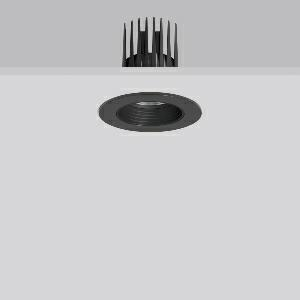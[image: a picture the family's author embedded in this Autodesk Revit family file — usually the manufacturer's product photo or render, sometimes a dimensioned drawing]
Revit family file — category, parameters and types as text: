
# Revit family: heledon_mini_e_901747_003_2_76_4866
name_source: partatom
category: Lighting Fixtures
units: mm (PartAtom-declared; Revit-internal decimal feet)

## family parameters
Cut with Voids When Loaded = No
Host = Face
Light Source = No
Part Type = Normal
Room Calculation Point = No
Round Connector Dimension = Use Diameter
Shared = No

## types (1)
- HELEDON mini E (1 x LED Modul 927, 1850 lm, 2700)
    Apparent Load = 20 VA
    Approval mark = CE
    CIE Flux Codes = 95 100 100 100 100
    Color Rendering = 92
    Color Temperature = 2700
    Default Elevation = 1800 mm
    Description = Series: HELEDON mini
Round recessed downlight. Housing: die-cast aluminium, powder-coated. Black plastic ring and recessed LED to prevent glare from the side. Optical assembly with lens made of plastic (polycarbonate) for the best homogeneous light distribution - can be changed without tools. Best colour rendering index Ra>90. Suitable for Recessed ceiling mounting. Installation without tools thanks to spring fastening system. Including separate LED converter with connecting cable 600 mm.High quality converter without flickering and stroboscopic effect. Through-wiring box (5 pole) available as accessory. The following accessories can be mounted without use of tools: interchangeable lenses, decorative glasses, honeycomb louvre, clear and frosted diffusers, white interchangeable plastic ring. 
Colour: deep black, matt (RAL 9005)
Diameter: 124 mm
Height: 3 mm
Cut-out diameter: 114 mm
Recess height: 170 mm
Luminaire: recess height: 120 mm
Lamp: LED
Socket: without socket
Colour temperature: 2700K
Colour rendering index (CRI): 92
System power: 20 W
Rated luminous flux: 1850 lm
Luminous efficiency: 93 lm/W
Control gear: Converter, dimmable, DALI
Protection class: II
Type of protection: IP 20
    Height = 0 mm  [stored 0 ft]
    Lamp = 1 x LED Modul 927
    Lamp Light Flux = 1850 lm
    Lamp count = 1
    Length = 124 mm  [stored 0.406824 ft]
    Lifetime = 50000 h
    Luminous efficacy = 93 lm/W
    Manufacturer = RZB
    ModVariant = No
    Model = 901747.003.2.76
    Mounting Place = Ceiling
    Mounting Type = Recessed
    Number of Poles = 1
    OnlyDefault = Yes
    Power Factor = 1
    Product Name = HELEDON mini E
    Product group = Recessed downlights
    ProductGroupID = 402
    Protection Class = Protection class II
    Protection Degree = IP 20
    RLX_Detail_Level = 1
    RLX_Emergency_Light_Flux = 0 lm
    RLX_Emergency_Type = 0
    RLX_Emergency_Type_DB = No
    RlxData = <blob elided: 133509 chars, md5=301091ec>
    Socket = socket
    Standby Power = 0 W
    System Light Flux = 1850 lm
    System Power = 20 W
    Type Comments = Product without accessories
    Type Image = 901656.003.jpg
    URL = http://relux.com
    VarID = ---
    Voltage = 230 V
    Voltage Range = 220-240 V
    Weight = 0.00 kg
    Width = 0 mm  [stored 0 ft]

note: [stored X ft] marks values corroborated as IEEE doubles in the binary element streams (Revit-internal decimal feet)

## geometry (parser evidence)
native form markers: Blend x4, Sweep x9
no freeform markers — native parametric forms only
